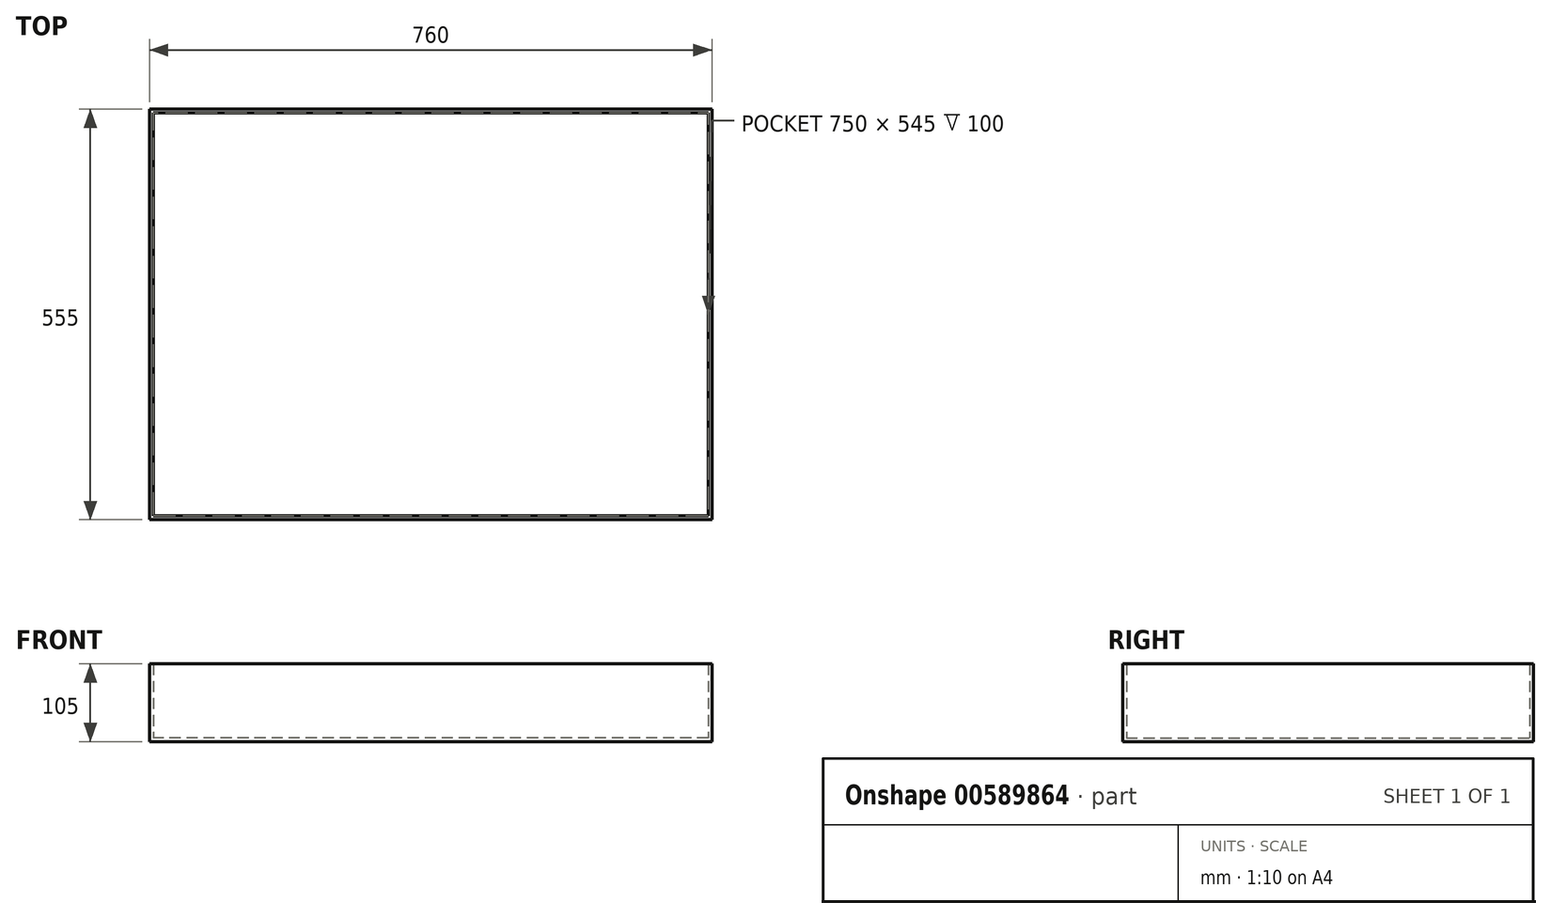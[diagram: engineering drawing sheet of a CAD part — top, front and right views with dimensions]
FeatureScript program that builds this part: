
annotation { "Feature Type Name" : "Feature", "Feature Type Description" : "" }
export const myFeature = defineFeature(function(context is Context, id is Id, definition is map)
    precondition{}
    {
        {
            var Q0;
            Q0=qCreatedBy(makeId("Top.planeOp"),FACE);
            var sketch = newSketch(context, id + "F0", { "sketchPlane" : qUnion([Q0])});
            skLineSegment(sketch, "E0.bottom", {"start": v(380, -275) * mm, "end": v(-380, -275) * mm});
            skLineSegment(sketch, "E0.top", {"start": v(375, 275) * mm, "end": v(-375, 275) * mm});
            skLineSegment(sketch, "E0.left", {"start": v(375, -270) * mm, "end": v(375, 275) * mm});
            skLineSegment(sketch, "E0.right", {"start": v(-375, -270) * mm, "end": v(-375, 275) * mm});
            skPoint(sketch, "E0.middle", {"position": v(0, 0) * mm});
            skLineSegment(sketch, "E1.0", {"start": v(380, 280) * mm, "end": v(-380, 280) * mm});
            skLineSegment(sketch, "E2.0", {"start": v(380, -275) * mm, "end": v(380, 280) * mm});
            skLineSegment(sketch, "E3.0", {"start": v(375, -270) * mm, "end": v(-375, -270) * mm});
            skLineSegment(sketch, "E4.0", {"start": v(-380, -275) * mm, "end": v(-380, 280) * mm});
            skSolve(sketch);
        }
        {
            var Q0;
            Q0=makeQuery(id+"F0.imprint","IMPRINT",FACE,{"disambiguationData":[TD([[makeQuery(id+"F0.imprint","IMPRINT",EDGE,{"derivedFrom":sQuery(id+"F0.wireOp",EDGE,"E0.top")}),1.0]])]});
            extrude(context, id + "F1", {"entities" : qUnion([Q0]), "depth" : 5 * mm, "offsetDistance" : 25 * mm});
        }
        {
            var Q0;
            Q0=makeQuery(id+"F0.imprint","IMPRINT",FACE,{"disambiguationData":[TD([[makeQuery(id+"F0.imprint","IMPRINT",EDGE,{"derivedFrom":sQuery(id+"F0.wireOp",EDGE,"E0.bottom")}),-1.0]])]});
            extrude(context, id + "F2", {"entities" : qUnion([Q0]), "operationType" : NewBodyOperationType.ADD, "depth" : (100 + 5) * mm, "offsetDistance" : 25 * mm});
        }
    });
